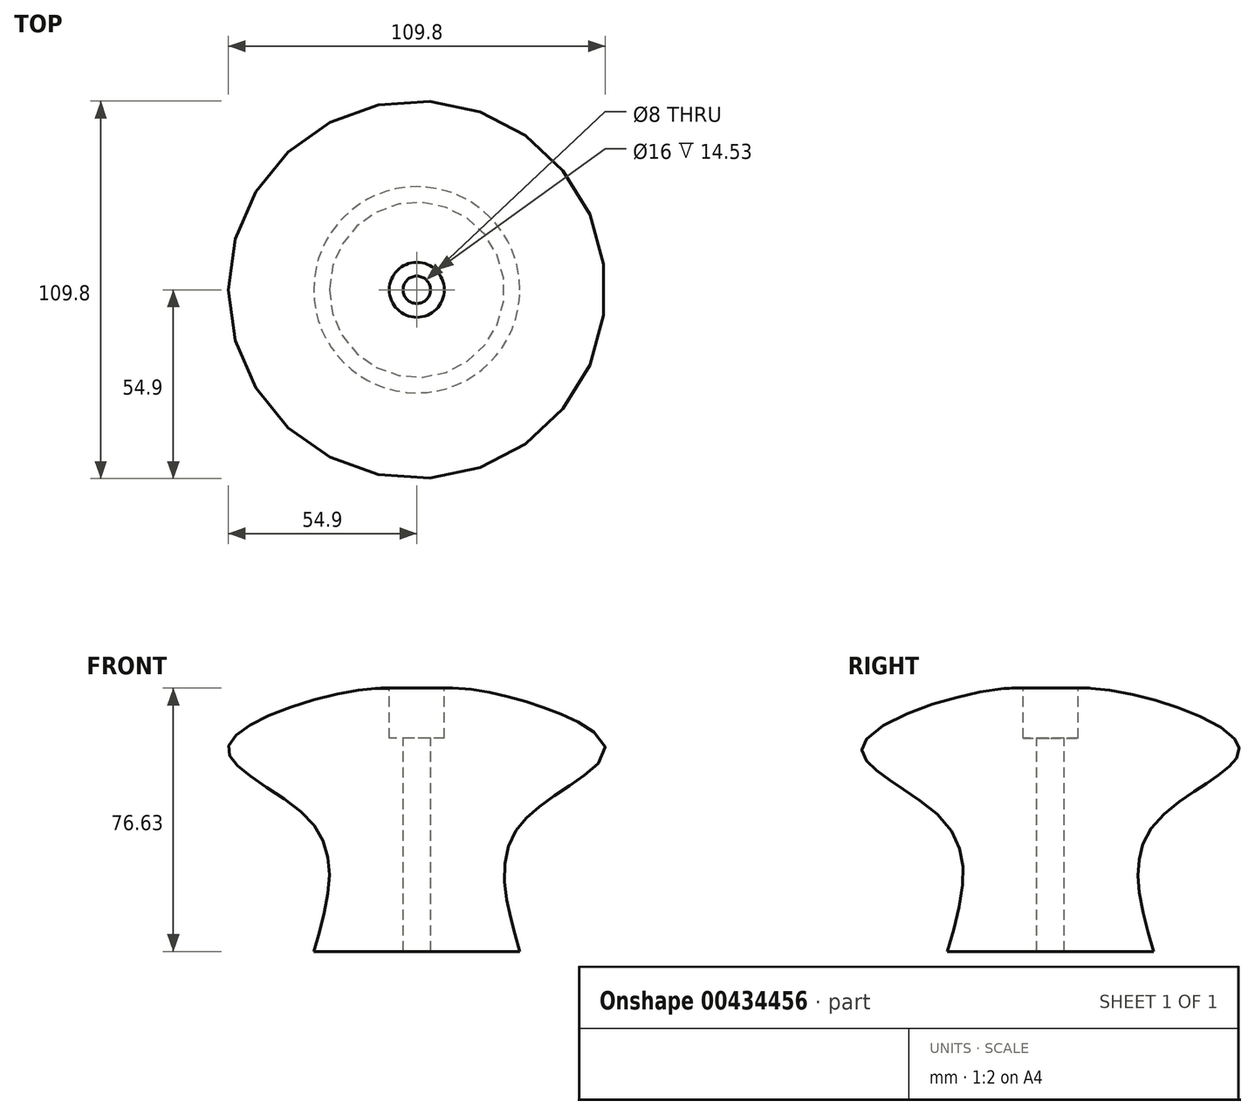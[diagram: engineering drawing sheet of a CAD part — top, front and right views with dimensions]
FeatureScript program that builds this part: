
annotation { "Feature Type Name" : "Feature", "Feature Type Description" : "" }
export const myFeature = defineFeature(function(context is Context, id is Id, definition is map)
    precondition{}
    {
        {
            var Q0;
            Q0=qCreatedBy(makeId("Front.planeOp"),FACE);
            var sketch = newSketch(context, id + "F0", { "sketchPlane" : qUnion([Q0])});
            skLineSegment(sketch, "E0", {"start": v(0, 0) * mm, "end": v(-30, 0) * mm});
            skLineSegment(sketch, "E1", {"start": v(0, 0) * mm, "end": v(0, 74.44) * mm});
            skPoint(sketch, "E2.3.internal.snap0", {"position": v(-15, 0) * mm});
            skFitSpline(sketch, "E2", {"points": [v(-30, 0) * mm, v(-30, 36.74) * mm, v(-54.88, 59.17) * mm, v(-15, 76.35) * mm, v(0, 74.44) * mm], "startDerivative": vector(43.34, 148.2) * mm, "endDerivative": vector(61.52, -24.1) * mm});
            skSolve(sketch);
        }
        {
            var Q0;
            Q0=makeQuery(id+"F0.imprint","IMPRINT",FACE,{"disambiguationData":[TD([[makeQuery(id+"F0.imprint","IMPRINT",EDGE,{"derivedFrom":sQuery(id+"F0.wireOp",EDGE,"E0")}),-1.0]])]});
            var Q1;
            Q1=sQuery(id+"F0.wireOp",EDGE,"E1");
            revolve(context, id + "F1", {"entities" : qUnion([Q0]), "axis" : qUnion([Q1]), "revolveType" : RevolveType.FULL});
        }
        {
            var Q0;
            Q0=qCreatedBy(makeId("Top.planeOp"),FACE);
            cPlane(context, id + "F2", {"entities" : qUnion([Q0]), "cplaneType" : CPlaneType.OFFSET, "offset" : 82 * mm, "width" : 150 * mm, "height" : 150 * mm});
        }
        {
            var Q0;
            Q0=qCreatedBy(id+"F2.planeOp",FACE);
            var sketch = newSketch(context, id + "F3", { "sketchPlane" : qUnion([Q0])});
            skCircle(sketch, "E3", {"center": v(0, 0) * mm, "radius": 4 * mm});
            skSolve(sketch);
        }
        {
            var Q0;
            Q0=makeQuery(id+"F3.imprint","IMPRINT",FACE,{"disambiguationData":[TD([[makeQuery(id+"F3.imprint","IMPRINT",EDGE,{"derivedFrom":sQuery(id+"F3.wireOp",EDGE,"E3")}),1.0]])]});
            extrude(context, id + "F4", {"entities" : qUnion([Q0]), "operationType" : NewBodyOperationType.REMOVE, "oppositeDirection" : true, "depth" : 128 * mm});
        }
        {
            var Q0;
            Q0=qCreatedBy(id+"F2.planeOp",FACE);
            var sketch = newSketch(context, id + "F5", { "sketchPlane" : qUnion([Q0])});
            skCircle(sketch, "E4", {"center": v(0, 0) * mm, "radius": 8 * mm});
            skSolve(sketch);
        }
        {
            var Q0;
            Q0=makeQuery(id+"F5.imprint","IMPRINT",FACE,{"disambiguationData":[TD([[makeQuery(id+"F5.imprint","IMPRINT",EDGE,{"derivedFrom":sQuery(id+"F5.wireOp",EDGE,"E4")}),1.0]])]});
            extrude(context, id + "F6", {"entities" : qUnion([Q0]), "operationType" : NewBodyOperationType.REMOVE, "oppositeDirection" : true, "depth" : 20 * mm});
        }
    });
